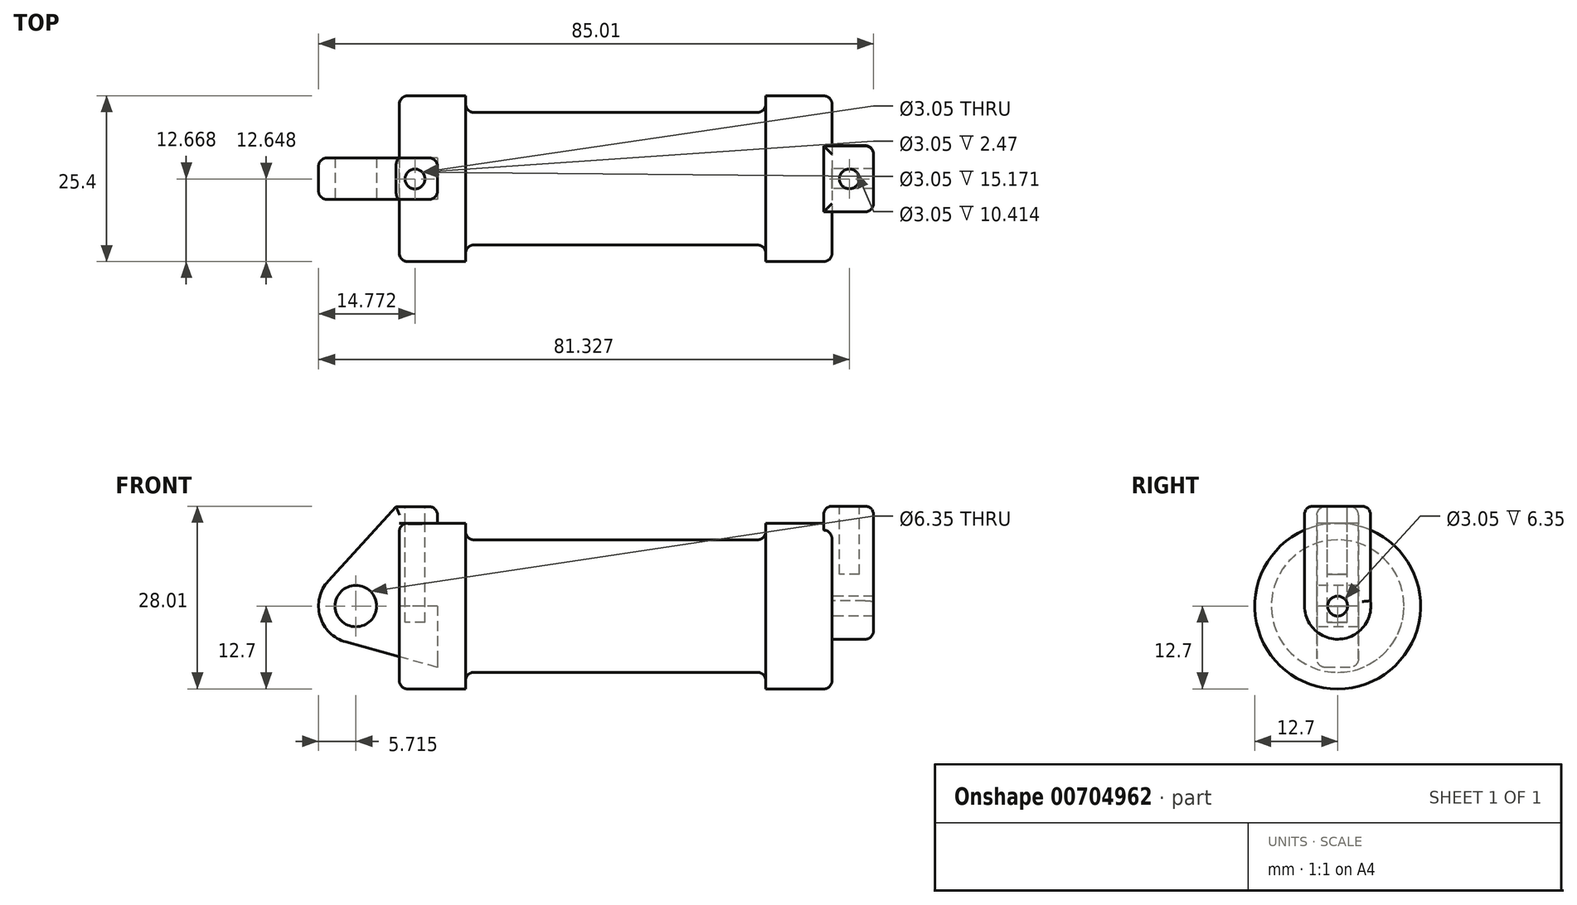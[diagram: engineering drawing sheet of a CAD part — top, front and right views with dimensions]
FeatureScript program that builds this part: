
annotation { "Feature Type Name" : "Feature", "Feature Type Description" : "" }
export const myFeature = defineFeature(function(context is Context, id is Id, definition is map)
    precondition{}
    {
        {
            var Q0;
            Q0=qCreatedBy(makeId("Front.planeOp"),FACE);
            var sketch = newSketch(context, id + "F0", { "sketchPlane" : qUnion([Q0])});
            skLineSegment(sketch, "E0", {"start": v(0, 0) * mm, "end": v(0, 12.7) * mm});
            skLineSegment(sketch, "E1", {"start": v(0, 12.7) * mm, "end": v(10.16, 12.7) * mm});
            skLineSegment(sketch, "E2", {"start": v(10.16, 12.7) * mm, "end": v(10.16, 10.16) * mm});
            skLineSegment(sketch, "E3", {"start": v(10.16, 10.16) * mm, "end": v(56.13, 10.16) * mm});
            skLineSegment(sketch, "E4", {"start": v(56.13, 10.16) * mm, "end": v(56.13, 12.7) * mm});
            skLineSegment(sketch, "E5", {"start": v(56.13, 12.7) * mm, "end": v(66.3, 12.7) * mm});
            skLineSegment(sketch, "E6", {"start": v(66.3, 12.7) * mm, "end": v(66.3, 0) * mm});
            skLineSegment(sketch, "E7", {"start": v(66.3, 0) * mm, "end": v(0, 0) * mm});
            skLineSegment(sketch, "E8", {"start": v(5.84, 15.24) * mm, "end": v(-0.5, 15.24) * mm});
            skLineSegment(sketch, "E9", {"start": v(-0.5, 15.24) * mm, "end": v(-10.88, 3.85) * mm});
            skLineSegment(sketch, "E10", {"start": v(0, 0) * mm, "end": v(-6.65, 0) * mm});
            skCircle(sketch, "E11", {"center": v(-6.65, 0) * mm, "radius": 5.72 * mm});
            skCircle(sketch, "E12", {"center": v(-6.65, 0) * mm, "radius": 3.18 * mm});
            skLineSegment(sketch, "E13", {"start": v(5.84, 15.24) * mm, "end": v(5.84, -9.4) * mm});
            skLineSegment(sketch, "E14", {"start": v(5.84, -9.4) * mm, "end": v(-8.18, -5.5) * mm});
            skSolve(sketch);
        }
        {
            var Q0;
            {var subQ0=sQuery(id+"F0.wireOp",EDGE,"E2");Q0=makeQuery(id+"F0.imprint","IMPRINT",FACE,{"disambiguationData":[TD([[makeQuery(id+"F0.imprint","IMPRINT",EDGE,{"derivedFrom":subQ0}),-1.0]])]});}
            var Q1;
            {var subQ0=sQuery(id+"F0.wireOp",EDGE,"E0");Q1=makeQuery(id+"F0.imprint","IMPRINT",FACE,{"disambiguationData":[TD([[makeQuery(id+"F0.imprint","IMPRINT",EDGE,{"derivedFrom":subQ0}),-1.0]])]});}
            var Q2;
            Q2=sQuery(id+"F0.wireOp",EDGE,"E7");
            revolve(context, id + "F1", {"entities" : qUnion([Q0, Q1]), "axis" : qUnion([Q2]), "revolveType" : RevolveType.FULL});
        }
        {
            var Q0;
            {var subQ5=sQuery(id+"F0.wireOp",EDGE,"E12");Q0=makeQuery(id+"F0.imprint","IMPRINT",FACE,{"disambiguationData":[TD([[makeQuery(id+"F0.imprint","IMPRINT",EDGE,{"derivedFrom":subQ5}),-1.0]])]});}
            var Q1;
            {var subQ0=sQuery(id+"F0.wireOp",EDGE,"E14");Q1=makeQuery(id+"F0.imprint","IMPRINT",FACE,{"disambiguationData":[TD([[makeQuery(id+"F0.imprint","IMPRINT",EDGE,{"derivedFrom":subQ0}),-1.0]])]});}
            var Q2;
            {var subQ1=sQuery(id+"F0.wireOp",EDGE,"E0");Q2=makeQuery(id+"F0.imprint","IMPRINT",FACE,{"disambiguationData":[TD([[makeQuery(id+"F0.imprint","IMPRINT",EDGE,{"derivedFrom":subQ1}),1.0]])]});}
            extrude(context, id + "F2", {"entities" : qUnion([Q0, Q1, Q2]), "endBound" : BoundingType.SYMMETRIC, "oppositeDirection" : true, "depth" : 6.35 * mm, "offsetDistance" : 25.4 * mm});
        }
        {
            var Q0;
            Q0=makeQuery(id+"F1.opRevolve","SWEPT_FACE",FACE,{"disambiguationData":[OSD([sQuery(id+"F0.wireOp",EDGE,"E6")])]});
            var sketch = newSketch(context, id + "F3", { "sketchPlane" : qUnion([Q0])});
            skCircle(sketch, "E15", {"center": v(0, 0) * mm, "radius": 1.52 * mm});
            skCircle(sketch, "E16", {"center": v(0, 0) * mm, "radius": 5.08 * mm});
            skLineSegment(sketch, "E17.bottom", {"start": v(-5.08, 0) * mm, "end": v(5.02, 0) * mm});
            skLineSegment(sketch, "E17.top", {"start": v(-5.08, 15.3) * mm, "end": v(5.02, 15.3) * mm});
            skLineSegment(sketch, "E17.left", {"start": v(-5.08, 0) * mm, "end": v(-5.08, 15.3) * mm});
            skLineSegment(sketch, "E17.right", {"start": v(5.02, 0) * mm, "end": v(5.02, 15.3) * mm});
            skSolve(sketch);
        }
        {
            var Q0;
            Q0 = qSketchRegion(id + "F3", true);
            extrude(context, id + "F4", {"entities" : qUnion([Q0]), "operationType" : NewBodyOperationType.ADD, "depth" : 6.35 * mm, "offsetDistance" : 25.4 * mm, "hasSecondDirection" : true, "secondDirectionOppositeDirection" : true, "secondDirectionDepth" : 1.27 * mm});
        }
        {
            var Q0;
            Q0=makeQuery(id+"F4.opExtrude","SWEPT_FACE",FACE,{"disambiguationData":[OSD([sQuery(id+"F3.wireOp",EDGE,"E17.top")])]});
            var sketch = newSketch(context, id + "F5", { "sketchPlane" : qUnion([Q0])});
            skCircle(sketch, "E18", {"center": v(68.96, -0.03) * mm, "radius": 1.52 * mm});
            skPoint(sketch, "E18.centerSnap0", {"position": v(72.64, -0.03) * mm});
            skCircle(sketch, "E19", {"center": v(2.4, -0.05) * mm, "radius": 1.52 * mm});
            skSolve(sketch);
        }
        {
            var Q0;
            Q0=makeQuery(id+"F5.imprint","IMPRINT",FACE,{"disambiguationData":[TD([[makeQuery(id+"F5.imprint","IMPRINT",EDGE,{"derivedFrom":sQuery(id+"F5.wireOp",EDGE,"E19")}),1.0]])]});
            extrude(context, id + "F6", {"entities" : qUnion([Q0]), "operationType" : NewBodyOperationType.REMOVE, "oppositeDirection" : true, "depth" : 17.78 * mm, "offsetDistance" : 25.4 * mm});
        }
        {
            var Q0;
            Q0=makeQuery(id+"F5.imprint","IMPRINT",FACE,{"disambiguationData":[TD([[makeQuery(id+"F5.imprint","IMPRINT",EDGE,{"derivedFrom":sQuery(id+"F5.wireOp",EDGE,"E19")}),1.0]])]});
            var Q1;
            Q1=makeQuery(id+"F5.imprint","IMPRINT",FACE,{"disambiguationData":[TD([[makeQuery(id+"F5.imprint","IMPRINT",EDGE,{"derivedFrom":sQuery(id+"F5.wireOp",EDGE,"E18")}),1.0]])]});
            extrude(context, id + "F7", {"entities" : qUnion([Q0, Q1]), "operationType" : NewBodyOperationType.REMOVE, "oppositeDirection" : true, "depth" : 10.4 * mm, "offsetDistance" : 25.4 * mm});
        }
        {
            var Q0;
            Q0=makeQuery(id+"F1.opRevolve","SWEPT_FACE",FACE,{"disambiguationData":[OSD([sQuery(id+"F0.wireOp",EDGE,"E3")])]});
            fillet(context, id + "F8", {"entities" : qUnion([Q0]), "radius" : 1.27 * mm, "tangentPropagation" : true, "allowEdgeOverflow" : false});
        }
        {
            var Q0;
            Q0=makeQuery(id+"F1.opRevolve","SWEPT_EDGE",EDGE,{"disambiguationData":[OSD([sQuery(id+"F0.wireOp",EDGE,"E0"),sQuery(id+"F0.wireOp",EDGE,"E1")])]});
            var Q1;
            Q1=makeQuery(id+"F1.opRevolve","SWEPT_EDGE",EDGE,{"disambiguationData":[OSD([sQuery(id+"F0.wireOp",EDGE,"E5"),sQuery(id+"F0.wireOp",EDGE,"E6")])]});
            fillet(context, id + "F9", {"entities" : qUnion([Q0, Q1]), "radius" : 1.27 * mm, "tangentPropagation" : true, "allowEdgeOverflow" : false});
        }
        {
            var Q0;
            Q0=makeQuery(id+"F2.opExtrude","CAP_EDGE",EDGE,{"disambiguationData":[OSD([sQuery(id+"F0.wireOp",EDGE,"E9")])],"isStart":true});
            var Q1;
            Q1=makeQuery(id+"F2.opExtrude","CAP_EDGE",EDGE,{"disambiguationData":[OSD([sQuery(id+"F0.wireOp",EDGE,"E9")])],"isStart":false});
            var Q2;
            Q2=makeQuery(id+"F2.opExtrude","CAP_EDGE",EDGE,{"disambiguationData":[OSD([sQuery(id+"F0.wireOp",EDGE,"E8")])],"isStart":false});
            var Q3;
            Q3=makeQuery(id+"F2.opExtrude","CAP_EDGE",EDGE,{"disambiguationData":[OSD([sQuery(id+"F0.wireOp",EDGE,"E8")])],"isStart":true});
            fillet(context, id + "F10", {"entities" : qUnion([Q0, Q1, Q2, Q3]), "radius" : 1.27 * mm, "tangentPropagation" : true, "allowEdgeOverflow" : false});
        }
        {
            var Q0;
            Q0=makeQuery(id+"F4.opExtrude","CAP_EDGE",EDGE,{"disambiguationData":[OSD([sQuery(id+"F3.wireOp",EDGE,"E17.left")])],"isStart":false});
            var Q1;
            Q1=makeQuery(id+"F4.opExtrude","CAP_EDGE",EDGE,{"disambiguationData":[OSD([sQuery(id+"F3.wireOp",EDGE,"E17.right")])],"isStart":false});
            var Q2;
            Q2=makeQuery(id+"F4.opExtrude","SWEPT_EDGE",EDGE,{"disambiguationData":[OSD([sQuery(id+"F3.wireOp",EDGE,"E17.top"),sQuery(id+"F3.wireOp",EDGE,"E17.left")])]});
            var Q3;
            Q3=makeQuery(id+"F4.opExtrude","SWEPT_EDGE",EDGE,{"disambiguationData":[OSD([sQuery(id+"F3.wireOp",EDGE,"E17.top"),sQuery(id+"F3.wireOp",EDGE,"E17.right")])]});
            var Q4;
            Q4=makeQuery(id+"F4.opExtrude","CAP_EDGE",EDGE,{"disambiguationData":[OSD([sQuery(id+"F3.wireOp",EDGE,"E17.top")])],"isStart":true});
            var Q5;
            Q5=makeQuery(id+"F4.opExtrude","CAP_EDGE",EDGE,{"disambiguationData":[OSD([sQuery(id+"F3.wireOp",EDGE,"E17.top")])],"isStart":false});
            var Q6;
            Q6=makeQuery(id+"F2.opExtrude","SWEPT_EDGE",EDGE,{"disambiguationData":[OSD([sQuery(id+"F0.wireOp",EDGE,"E8"),sQuery(id+"F0.wireOp",EDGE,"E13")])]});
            fillet(context, id + "F11", {"entities" : qUnion([Q0, Q1, Q2, Q3, Q4, Q5, Q6]), "radius" : 1.27 * mm, "tangentPropagation" : true, "allowEdgeOverflow" : false});
        }
    });
